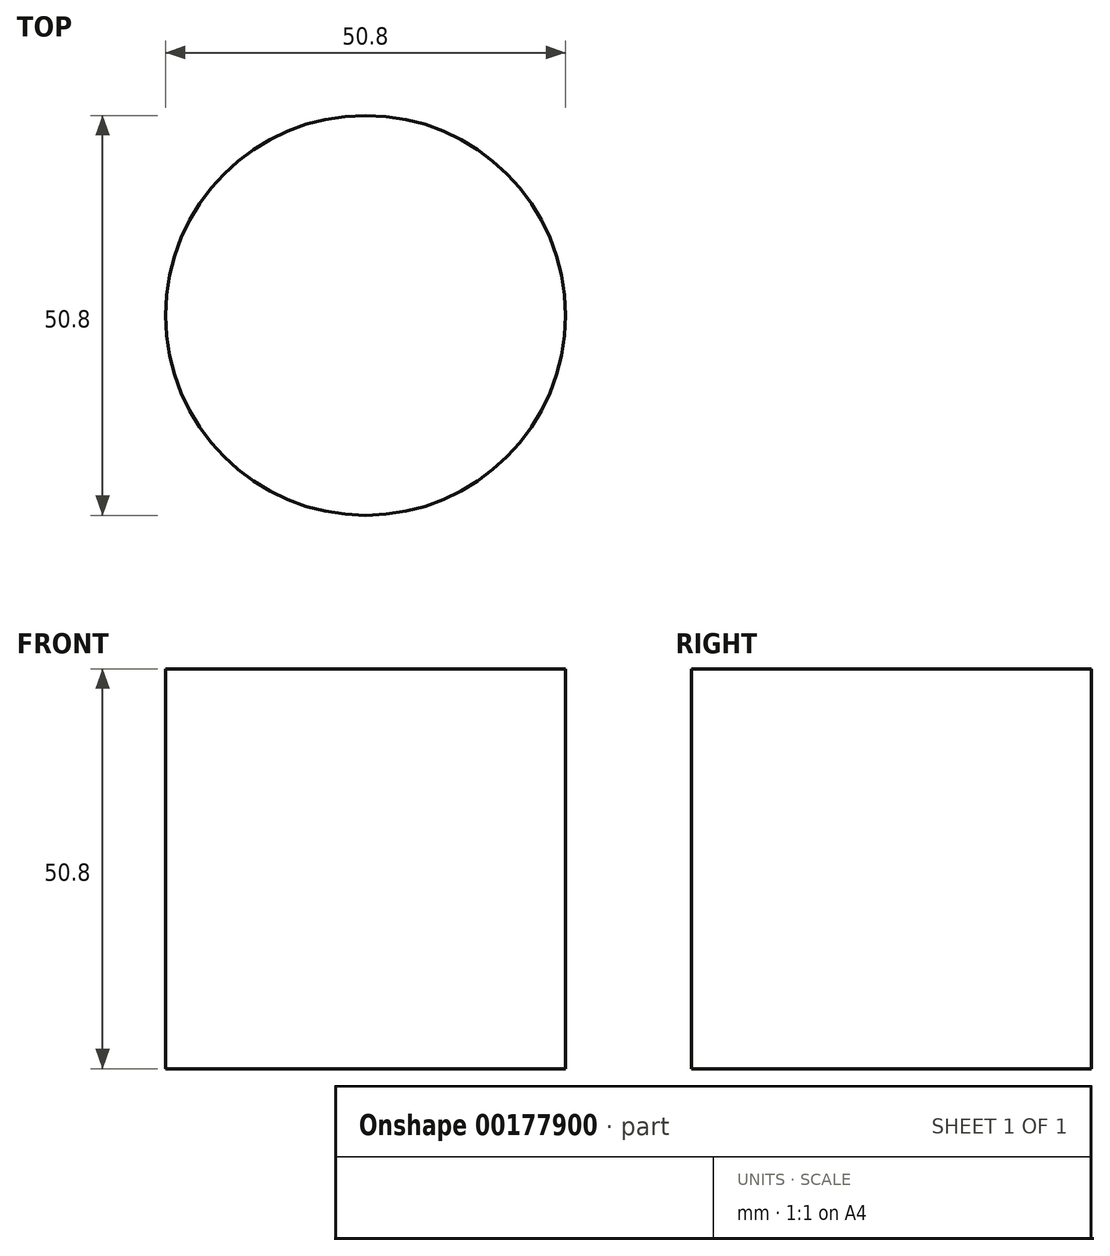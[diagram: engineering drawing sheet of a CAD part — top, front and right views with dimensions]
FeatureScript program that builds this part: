
annotation { "Feature Type Name" : "Feature", "Feature Type Description" : "" }
export const myFeature = defineFeature(function(context is Context, id is Id, definition is map)
    precondition{}
    {
        {
            var Q0;
            Q0=qCreatedBy(makeId("Top.planeOp"),FACE);
            var sketch = newSketch(context, id + "F0", { "sketchPlane" : qUnion([Q0])});
            skCircle(sketch, "E0", {"center": v(-158.38, 0) * mm, "radius": 25.4 * mm});
            skLineSegment(sketch, "E1.bottom", {"start": v(58.76, 131.86) * mm, "end": v(131.14, 131.86) * mm});
            skLineSegment(sketch, "E1.top", {"start": v(58.76, 56.62) * mm, "end": v(131.14, 56.62) * mm});
            skLineSegment(sketch, "E1.left", {"start": v(58.76, 131.86) * mm, "end": v(58.76, 56.62) * mm});
            skLineSegment(sketch, "E1.right", {"start": v(131.14, 131.86) * mm, "end": v(131.14, 56.62) * mm});
            skLineSegment(sketch, "E2.bottom", {"start": v(121.72, -41.2) * mm, "end": v(204.53, -41.2) * mm});
            skLineSegment(sketch, "E2.top", {"start": v(121.72, -138.75) * mm, "end": v(204.53, -138.75) * mm});
            skLineSegment(sketch, "E2.left", {"start": v(121.72, -41.2) * mm, "end": v(121.72, -138.75) * mm});
            skLineSegment(sketch, "E2.right", {"start": v(204.53, -41.2) * mm, "end": v(204.53, -138.75) * mm});
            skSolve(sketch);
        }
        {
            var Q0;
            Q0=makeQuery(id+"F0.imprint","IMPRINT",FACE,{"disambiguationData":[TD([[makeQuery(id+"F0.imprint","IMPRINT",EDGE,{"derivedFrom":sQuery(id+"F0.wireOp",EDGE,"E0")}),1.0]])]});
            extrude(context, id + "F1", {"entities" : qUnion([Q0]), "depth" : 50.8 * mm});
        }
    });
